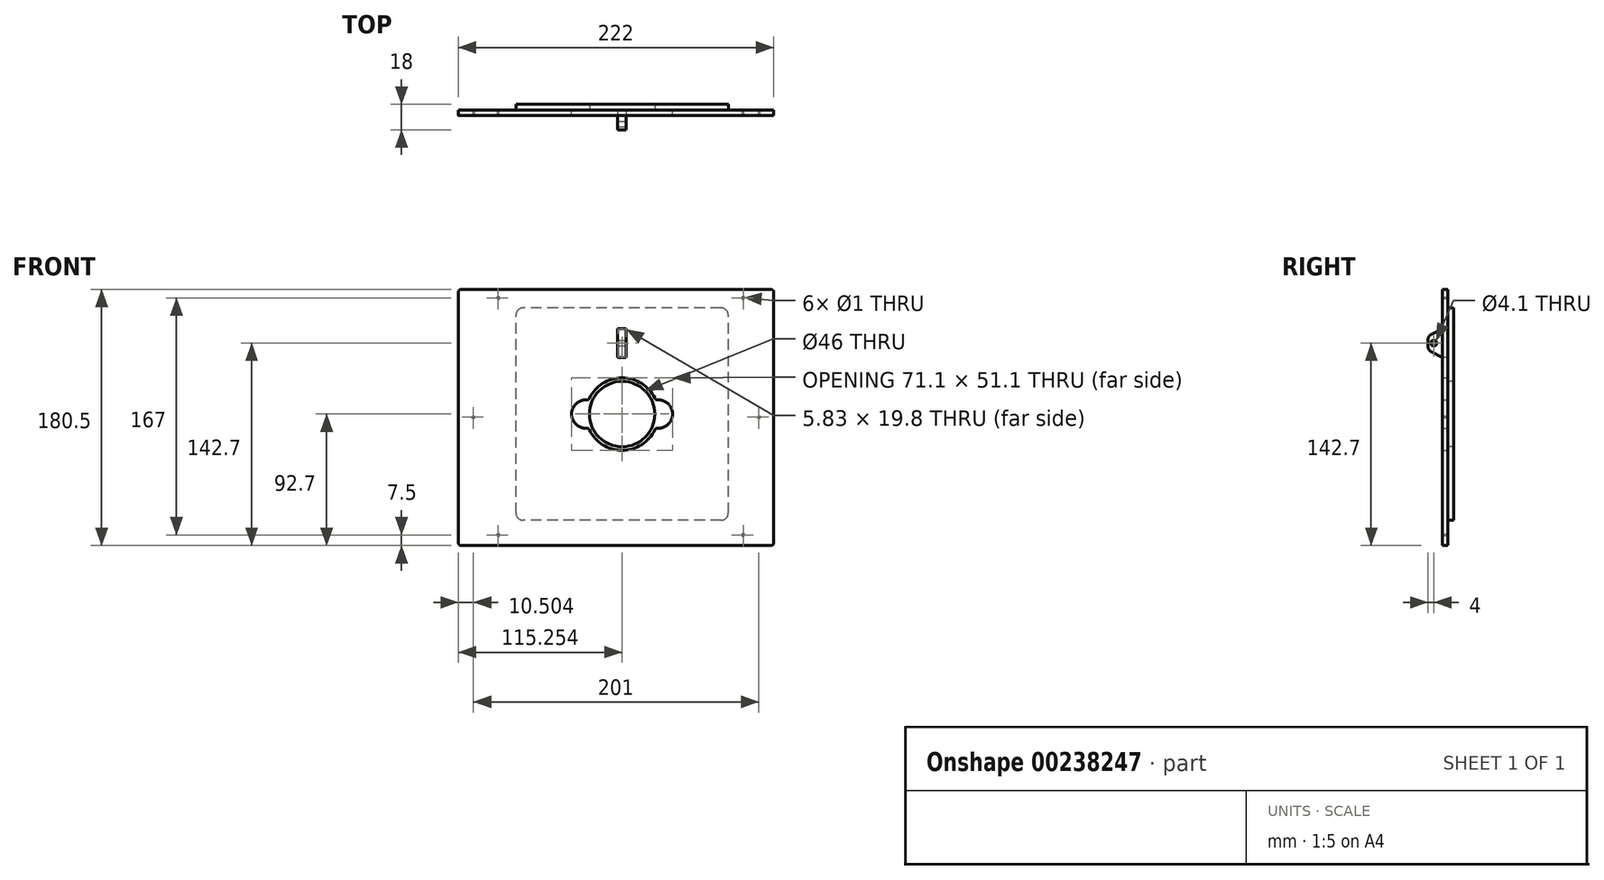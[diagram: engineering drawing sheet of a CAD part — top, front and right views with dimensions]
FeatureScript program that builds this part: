
annotation { "Feature Type Name" : "Feature", "Feature Type Description" : "" }
export const myFeature = defineFeature(function(context is Context, id is Id, definition is map)
    precondition{}
    {
        {
            var Q0;
            Q0=qCreatedBy(makeId("Front.planeOp"),FACE);
            var sketch = newSketch(context, id + "F0", { "sketchPlane" : qUnion([Q0])});
            skLineSegment(sketch, "E0.bottom", {"start": v(-37.98, 90.25) * mm, "end": v(-255.98, 90.25) * mm});
            skLineSegment(sketch, "E0.top", {"start": v(-37.98, -90.25) * mm, "end": v(-255.98, -90.25) * mm});
            skLineSegment(sketch, "E0.left", {"start": v(-35.98, 88.25) * mm, "end": v(-35.98, -88.25) * mm});
            skLineSegment(sketch, "E0.right", {"start": v(-257.98, 88.25) * mm, "end": v(-257.98, -88.25) * mm});
            skLineSegment(sketch, "E1.bottom", {"start": v(-57.48, 84.25) * mm, "end": v(-229.98, 84.25) * mm, "construction": true});
            skLineSegment(sketch, "E1.top", {"start": v(-57.48, -82.75) * mm, "end": v(-229.98, -82.75) * mm, "construction": true});
            skLineSegment(sketch, "E1.left", {"start": v(-57.48, 84.25) * mm, "end": v(-57.48, -82.75) * mm, "construction": true});
            skLineSegment(sketch, "E1.right", {"start": v(-229.98, 84.25) * mm, "end": v(-229.98, -82.75) * mm, "construction": true});
            skPoint(sketch, "E1.middle", {"position": v(-143.48, 0) * mm});
            skLineSegment(sketch, "E2", {"start": v(-257.98, 0) * mm, "end": v(-35.98, 0) * mm, "construction": true});
            skLineSegment(sketch, "E3.bottom", {"start": v(-67.73, 77.45) * mm, "end": v(-217.73, 77.45) * mm, "construction": true});
            skLineSegment(sketch, "E3.top", {"start": v(-67.73, -72.55) * mm, "end": v(-217.73, -72.55) * mm, "construction": true});
            skLineSegment(sketch, "E3.left", {"start": v(-67.73, 77.45) * mm, "end": v(-67.73, -72.55) * mm, "construction": true});
            skLineSegment(sketch, "E3.right", {"start": v(-217.73, 77.45) * mm, "end": v(-217.73, -72.55) * mm, "construction": true});
            skPoint(sketch, "E3.middle", {"position": v(-142.73, 2.45) * mm});
            skPoint(sketch, "E4.visualSharp", {"position": v(-257.98, 90.25) * mm});
            skArc(sketch, "E4.filletArc", {"start": v(-255.98, 90.25) * mm, "mid": v(-257.4, 89.66) * mm, "end": v(-257.98, 88.25) * mm});
            skPoint(sketch, "E5.visualSharp", {"position": v(-257.98, -90.25) * mm});
            skArc(sketch, "E5.filletArc", {"start": v(-257.98, -88.25) * mm, "mid": v(-257.4, -89.66) * mm, "end": v(-255.98, -90.25) * mm});
            skPoint(sketch, "E6.visualSharp", {"position": v(-35.98, 90.25) * mm});
            skArc(sketch, "E6.filletArc", {"start": v(-35.98, 88.25) * mm, "mid": v(-36.56, 89.66) * mm, "end": v(-37.98, 90.25) * mm});
            skPoint(sketch, "E7.visualSharp", {"position": v(-35.98, -90.25) * mm});
            skArc(sketch, "E7.filletArc", {"start": v(-37.98, -90.25) * mm, "mid": v(-36.56, -89.66) * mm, "end": v(-35.98, -88.25) * mm});
            skCircle(sketch, "E8", {"center": v(-229.98, 84.25) * mm, "radius": 0.5 * mm});
            skCircle(sketch, "E9", {"center": v(-229.98, -82.75) * mm, "radius": 0.5 * mm});
            skCircle(sketch, "E10", {"center": v(-57.48, 84.25) * mm, "radius": 0.5 * mm});
            skCircle(sketch, "E11", {"center": v(-57.48, -82.75) * mm, "radius": 0.5 * mm});
            skLineSegment(sketch, "E12", {"start": v(-168.28, 2.45) * mm, "end": v(-117.18, 2.45) * mm, "construction": true});
            skArc(sketch, "E13", {"start": v(-167.66, 12.43) * mm, "mid": v(-178.28, 2.45) * mm, "end": v(-167.66, -7.53) * mm});
            skArc(sketch, "E14", {"start": v(-117.8, -7.53) * mm, "mid": v(-107.18, 2.45) * mm, "end": v(-117.8, 12.43) * mm});
            skArc(sketch, "E15.trimOffspring", {"start": v(-165.74, -8.66) * mm, "mid": v(-142.73, -23.1) * mm, "end": v(-119.72, -8.66) * mm});
            skArc(sketch, "E16.trimOffspring", {"start": v(-119.72, 13.56) * mm, "mid": v(-142.73, 28) * mm, "end": v(-165.74, 13.56) * mm});
            skPoint(sketch, "E17.visualSharp", {"position": v(-166.32, 12.26) * mm});
            skArc(sketch, "E17.filletArc", {"start": v(-167.66, 12.43) * mm, "mid": v(-166.53, 12.7) * mm, "end": v(-165.74, 13.56) * mm});
            skPoint(sketch, "E18.visualSharp", {"position": v(-166.32, -7.36) * mm});
            skArc(sketch, "E18.filletArc", {"start": v(-165.74, -8.66) * mm, "mid": v(-166.53, -7.8) * mm, "end": v(-167.66, -7.53) * mm});
            skPoint(sketch, "E19.visualSharp", {"position": v(-119.13, -7.36) * mm});
            skArc(sketch, "E19.filletArc", {"start": v(-117.8, -7.53) * mm, "mid": v(-118.93, -7.8) * mm, "end": v(-119.72, -8.66) * mm});
            skPoint(sketch, "E20.visualSharp", {"position": v(-119.13, 12.26) * mm});
            skArc(sketch, "E20.filletArc", {"start": v(-119.72, 13.56) * mm, "mid": v(-118.93, 12.7) * mm, "end": v(-117.8, 12.43) * mm});
            skLineSegment(sketch, "E21.bottom", {"start": v(-139.81, 42.55) * mm, "end": v(-145.64, 42.55) * mm});
            skLineSegment(sketch, "E21.top", {"start": v(-139.81, 62.35) * mm, "end": v(-145.64, 62.35) * mm});
            skLineSegment(sketch, "E21.left", {"start": v(-139.81, 42.55) * mm, "end": v(-139.81, 62.35) * mm});
            skLineSegment(sketch, "E21.right", {"start": v(-145.64, 42.55) * mm, "end": v(-145.64, 62.35) * mm});
            skPoint(sketch, "E21.middle", {"position": v(-142.73, 52.45) * mm});
            skSolve(sketch);
        }
        {
            var Q0;
            Q0=qSketchRegion(id+"F0",true);
            extrude(context, id + "F1", {"entities" : qUnion([Q0]), "depth" : 4 * mm});
        }
        {
            var Q0;
            Q0=makeQuery(id+"F1.opExtrude","CAP_FACE",FACE,{"disambiguationData":[OSD([sQuery(id+"F0.wireOp",EDGE,"E0.bottom"),sQuery(id+"F0.wireOp",EDGE,"E0.top"),sQuery(id+"F0.wireOp",EDGE,"E0.left"),sQuery(id+"F0.wireOp",EDGE,"E0.right"),sQuery(id+"F0.wireOp",EDGE,"E4.filletArc"),sQuery(id+"F0.wireOp",EDGE,"E5.filletArc"),sQuery(id+"F0.wireOp",EDGE,"E6.filletArc"),sQuery(id+"F0.wireOp",EDGE,"E7.filletArc"),sQuery(id+"F0.wireOp",EDGE,"E8"),sQuery(id+"F0.wireOp",EDGE,"E9"),sQuery(id+"F0.wireOp",EDGE,"E10"),sQuery(id+"F0.wireOp",EDGE,"E11"),sQuery(id+"F0.wireOp",EDGE,"E13"),sQuery(id+"F0.wireOp",EDGE,"E14"),sQuery(id+"F0.wireOp",EDGE,"E15.trimOffspring"),sQuery(id+"F0.wireOp",EDGE,"E16.trimOffspring"),sQuery(id+"F0.wireOp",EDGE,"E17.filletArc"),sQuery(id+"F0.wireOp",EDGE,"E18.filletArc"),sQuery(id+"F0.wireOp",EDGE,"E19.filletArc"),sQuery(id+"F0.wireOp",EDGE,"E20.filletArc"),sQuery(id+"F0.wireOp",EDGE,"E21.bottom"),sQuery(id+"F0.wireOp",EDGE,"E21.top"),sQuery(id+"F0.wireOp",EDGE,"E21.left"),sQuery(id+"F0.wireOp",EDGE,"E21.right")])],"isStart":true});
            var sketch = newSketch(context, id + "F2", { "sketchPlane" : qUnion([Q0])});
            skArc(sketch, "E22.0", {"start": v(165.74, -8.66) * mm, "mid": v(142.73, -23.1) * mm, "end": v(119.72, -8.66) * mm, "construction": true});
            skCircle(sketch, "E23", {"center": v(142.73, 2.45) * mm, "radius": 23 * mm});
            skLineSegment(sketch, "E24.bottom", {"start": v(72.98, -72.3) * mm, "end": v(212.48, -72.3) * mm});
            skLineSegment(sketch, "E24.top", {"start": v(72.98, 77.2) * mm, "end": v(212.48, 77.2) * mm});
            skLineSegment(sketch, "E24.left", {"start": v(67.98, -67.3) * mm, "end": v(67.98, 72.2) * mm});
            skLineSegment(sketch, "E24.right", {"start": v(217.48, -67.3) * mm, "end": v(217.48, 72.2) * mm});
            skPoint(sketch, "E25.visualSharp", {"position": v(217.48, -72.3) * mm});
            skArc(sketch, "E25.filletArc", {"start": v(212.48, -72.3) * mm, "mid": v(216.01, -70.84) * mm, "end": v(217.48, -67.3) * mm});
            skPoint(sketch, "E26.visualSharp", {"position": v(217.48, 77.2) * mm});
            skArc(sketch, "E26.filletArc", {"start": v(217.48, 72.2) * mm, "mid": v(216.01, 75.74) * mm, "end": v(212.48, 77.2) * mm});
            skPoint(sketch, "E27.visualSharp", {"position": v(67.98, 77.2) * mm});
            skArc(sketch, "E27.filletArc", {"start": v(72.98, 77.2) * mm, "mid": v(69.44, 75.74) * mm, "end": v(67.98, 72.2) * mm});
            skPoint(sketch, "E28.visualSharp", {"position": v(67.98, -72.3) * mm});
            skArc(sketch, "E28.filletArc", {"start": v(67.98, -67.3) * mm, "mid": v(69.44, -70.84) * mm, "end": v(72.98, -72.3) * mm});
            skSolve(sketch);
        }
        {
            var Q0;
            Q0=qSketchRegion(id+"F2",true);
            extrude(context, id + "F3", {"entities" : qUnion([Q0]), "depth" : 4 * mm});
        }
        {
            var Q0;
            Q0=makeQuery(id+"F1.opExtrude","SWEPT_FACE",FACE,{"disambiguationData":[OSD([sQuery(id+"F0.wireOp",EDGE,"E21.left")])]});
            var sketch = newSketch(context, id + "F4", { "sketchPlane" : qUnion([Q0])});
            skLineSegment(sketch, "E29.0", {"start": v(0, 42.55) * mm, "end": v(0, 62.35) * mm});
            skLineSegment(sketch, "E30", {"start": v(0, 62.35) * mm, "end": v(0, 62.55) * mm});
            skLineSegment(sketch, "E31", {"start": v(0, 42.55) * mm, "end": v(0, 42.35) * mm});
            skPoint(sketch, "E32.endSnap0", {"position": v(0, 52.45) * mm});
            skLineSegment(sketch, "E33", {"start": v(0, 62.55) * mm, "end": v(4, 62.55) * mm});
            skLineSegment(sketch, "E34", {"start": v(4, 62.55) * mm, "end": v(11.82, 58.56) * mm});
            skLineSegment(sketch, "E35", {"start": v(0, 42.35) * mm, "end": v(4, 42.35) * mm});
            skLineSegment(sketch, "E36", {"start": v(4, 42.35) * mm, "end": v(11.82, 46.34) * mm});
            skLineSegment(sketch, "E37", {"start": v(14, 52.45) * mm, "end": v(0, 52.45) * mm, "construction": true});
            skLineSegment(sketch, "E38", {"start": v(14, 55) * mm, "end": v(14, 49.9) * mm});
            skCircle(sketch, "E39", {"center": v(10, 52.45) * mm, "radius": 2.05 * mm});
            skPoint(sketch, "E40.visualSharp", {"position": v(14, 57.45) * mm});
            skArc(sketch, "E40.filletArc", {"start": v(14, 55) * mm, "mid": v(13.41, 57.09) * mm, "end": v(11.82, 58.56) * mm});
            skPoint(sketch, "E41.visualSharp", {"position": v(14, 47.45) * mm});
            skArc(sketch, "E41.filletArc", {"start": v(11.82, 46.34) * mm, "mid": v(13.41, 47.81) * mm, "end": v(14, 49.9) * mm});
            skSolve(sketch);
        }
        {
            var Q0;
            Q0=makeQuery(id+"F4.imprint","IMPRINT",FACE,{"disambiguationData":[TD([[makeQuery(id+"F4.imprint","IMPRINT",EDGE,{"derivedFrom":sQuery(id+"F4.wireOp",EDGE,"E30")}),-1.0]])]});
            var Q1;
            Q1=makeQuery(id+"F4.imprint","IMPRINT",FACE,{"disambiguationData":[TD([[makeQuery(id+"F4.imprint","IMPRINT",EDGE,{"derivedFrom":sQuery(id+"F4.wireOp",EDGE,"E29.0")}),-1.0]])]});
            extrude(context, id + "F5", {"entities" : qUnion([Q0, Q1]), "depth" : 6 * mm});
        }
        {
            var Q0;
            Q0=makeQuery(id+"F1.opExtrude","CAP_FACE",FACE,{"disambiguationData":[OSD([sQuery(id+"F0.wireOp",EDGE,"E0.bottom"),sQuery(id+"F0.wireOp",EDGE,"E0.top"),sQuery(id+"F0.wireOp",EDGE,"E0.left"),sQuery(id+"F0.wireOp",EDGE,"E0.right"),sQuery(id+"F0.wireOp",EDGE,"E4.filletArc"),sQuery(id+"F0.wireOp",EDGE,"E5.filletArc"),sQuery(id+"F0.wireOp",EDGE,"E6.filletArc"),sQuery(id+"F0.wireOp",EDGE,"E7.filletArc"),sQuery(id+"F0.wireOp",EDGE,"E8"),sQuery(id+"F0.wireOp",EDGE,"E9"),sQuery(id+"F0.wireOp",EDGE,"E10"),sQuery(id+"F0.wireOp",EDGE,"E11"),sQuery(id+"F0.wireOp",EDGE,"E13"),sQuery(id+"F0.wireOp",EDGE,"E14"),sQuery(id+"F0.wireOp",EDGE,"E15.trimOffspring"),sQuery(id+"F0.wireOp",EDGE,"E16.trimOffspring"),sQuery(id+"F0.wireOp",EDGE,"E17.filletArc"),sQuery(id+"F0.wireOp",EDGE,"E18.filletArc"),sQuery(id+"F0.wireOp",EDGE,"E19.filletArc"),sQuery(id+"F0.wireOp",EDGE,"E20.filletArc"),sQuery(id+"F0.wireOp",EDGE,"E21.bottom"),sQuery(id+"F0.wireOp",EDGE,"E21.top"),sQuery(id+"F0.wireOp",EDGE,"E21.left"),sQuery(id+"F0.wireOp",EDGE,"E21.right")])],"isStart":false});
            var sketch = newSketch(context, id + "F6", { "sketchPlane" : qUnion([Q0])});
            skLineSegment(sketch, "E42.0", {"start": v(-37.98, 90.25) * mm, "end": v(-255.98, 90.25) * mm, "construction": true});
            skLineSegment(sketch, "E42.1", {"start": v(-35.98, 88.25) * mm, "end": v(-35.98, -88.25) * mm, "construction": true});
            skCircle(sketch, "E43", {"center": v(-247.48, 0.25) * mm, "radius": 0.5 * mm});
            skCircle(sketch, "E44", {"center": v(-46.48, 0.25) * mm, "radius": 0.5 * mm});
            skLineSegment(sketch, "E45", {"start": v(-247.48, 0.25) * mm, "end": v(-46.48, 0.25) * mm, "construction": true});
            skLineSegment(sketch, "E46", {"start": v(-146.98, 90.25) * mm, "end": v(-146.98, 0.25) * mm, "construction": true});
            skSolve(sketch);
        }
        {
            var Q0;
            Q0=qSketchRegion(id+"F6",true);
            extrude(context, id + "F7", {"entities" : qUnion([Q0]), "operationType" : NewBodyOperationType.REMOVE, "oppositeDirection" : true, "depth" : 25 * mm});
        }
    });
